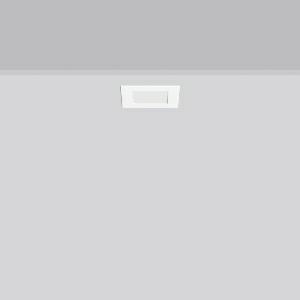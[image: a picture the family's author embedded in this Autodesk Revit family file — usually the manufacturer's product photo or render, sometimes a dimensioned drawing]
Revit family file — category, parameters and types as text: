
# Revit family: toledo_flat_square_e_901485_002_1_76_4028
name_source: partatom
category: Lighting Fixtures
units: mm (PartAtom-declared; Revit-internal decimal feet)

## family parameters
Cut with Voids When Loaded = No
Host = Face
Light Source = No
Part Type = Normal
Room Calculation Point = No
Round Connector Dimension = Use Diameter
Shared = No

## types (1)
- TOLEDO FLAT square E (1 x LED Modul 840, 430 lm, 4000)
    Apparent Load = 5 VA
    CIE Flux Codes = 49 80 96 100 100
    Color Rendering = 80
    Color Temperature = 4000
    Default Elevation = 1800 mm
    Description = Series: TOLEDO FLAT square
Ultra thin recessed downlight. Housing: die-cast aluminium. Light guide and diffuser made of non-yellowing PMMA, opal matt. Ceiling installation with spring system. Mounting depth depends on ceiling strength. Suitable for through-wiring with separately available accessories. Surface mounted housing as accessory for all sizes. Retrofittable decorative cylinders made of chintz fabric as accessory, optional with satin finish plastic diffuser. Through-wiring box (5 pole) available as accessory. 
Colour: white
Length: 110 mm
Width: 110 mm
Height: 3 mm
Cut-out length: 96 mm
Cut-out width: 96 mm
Recess height: 31-56 mm
Luminaire: recess height: 31-51 mm
Lamp: LED
Socket: without socket
Colour temperature: 4000K
Colour rendering index (CRI): 80
System power: 5 W
Rated luminous flux: 430 lm
Luminous efficiency: 86 lm/W
Control gear: Converter, dimmable, DALI
Protection class: II
Type of protection: IP 54
    Height = 0 mm  [stored 0 ft]
    Lamp = 1 x LED Modul 840
    Lamp Light Flux = 430 lm
    Lamp count = 1
    Length = 110 mm
    Lifetime = 50000 h
    Luminous efficacy = 86 lm/W
    Manufacturer = RZB
    ModVariant = No
    Model = 901485.002.1.76
    Mounting Place = Ceiling
    Mounting Type = Recessed
    Number of Poles = 1
    OnlyDefault = Yes
    Power Factor = 1
    Product Name = TOLEDO FLAT square E
    Product group = Recessed downlights
    ProductGroupID = 402
    Protection Class = Protection class II
    Protection Degree = IP 20
    RLX_Detail_Level = 1
    RLX_Emergency_Light_Flux = 0 lm
    RLX_Emergency_Type = 0
    RLX_Emergency_Type_DB = No
    RlxData = <blob elided: 57657 chars, md5=e6ae52b3>
    Socket = socket
    Standby Power = 0 W
    System Light Flux = 430 lm
    System Power = 5 W
    Type Comments = Product without accessories
    Type Image = 901485.002.jpg
    URL = http://relux.com
    VarID = ---
    Voltage = 230 V
    Voltage Range = 220-240 V
    Weight = 0.00 kg
    Width = 110 mm

note: [stored X ft] marks values corroborated as IEEE doubles in the binary element streams (Revit-internal decimal feet)

## geometry (parser evidence)
native form markers: Blend x4, Sweep x12
no freeform markers — native parametric forms only
